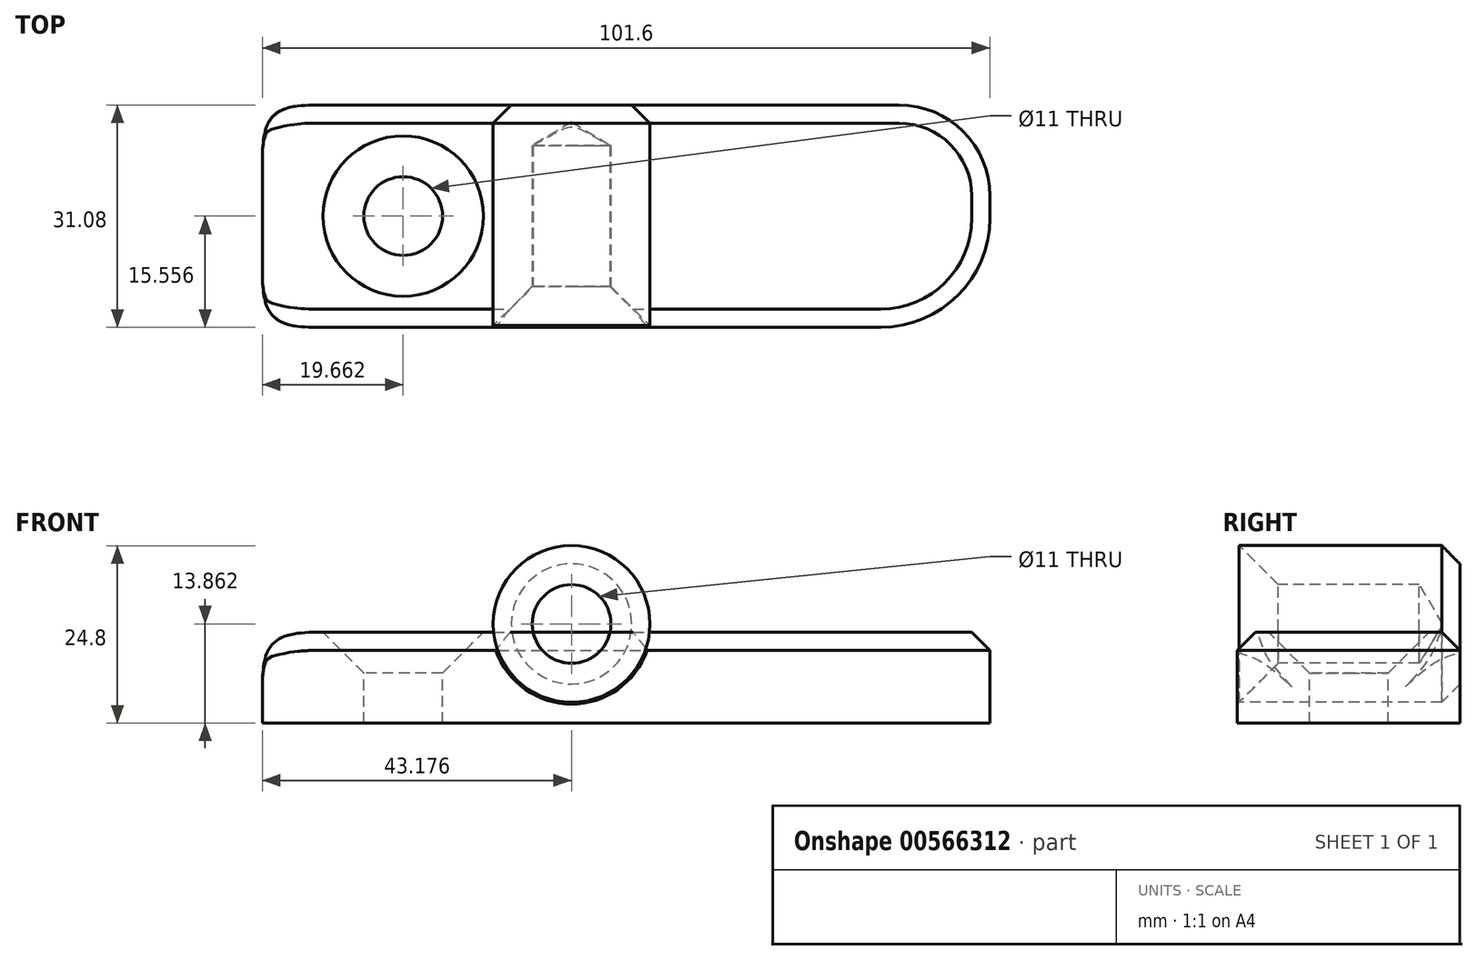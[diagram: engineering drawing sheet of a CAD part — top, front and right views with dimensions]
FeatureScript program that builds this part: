
annotation { "Feature Type Name" : "Feature", "Feature Type Description" : "" }
export const myFeature = defineFeature(function(context is Context, id is Id, definition is map)
    precondition{}
    {
        {
            var Q0;
            Q0=qCreatedBy(makeId("Top.planeOp"),FACE);
            var sketch = newSketch(context, id + "F0", { "sketchPlane" : qUnion([Q0])});
            skLineSegment(sketch, "E0.bottom", {"start": v(-114.14, 31.08) * mm, "end": v(-25.24, 31.08) * mm});
            skLineSegment(sketch, "E0.top", {"start": v(-114.14, 0) * mm, "end": v(-27.78, 0) * mm});
            skLineSegment(sketch, "E0.left", {"start": v(-114.14, 31.08) * mm, "end": v(-114.14, 0) * mm});
            skLineSegment(sketch, "E0.right", {"start": v(-12.54, 18.38) * mm, "end": v(-12.54, 15.24) * mm});
            skPoint(sketch, "E1.visualSharp", {"position": v(-12.54, 31.08) * mm});
            skArc(sketch, "E1.filletArc", {"start": v(-12.54, 18.38) * mm, "mid": v(-16.26, 27.36) * mm, "end": v(-25.24, 31.08) * mm});
            skPoint(sketch, "E2.visualSharp", {"position": v(-12.54, 0) * mm});
            skArc(sketch, "E2.filletArc", {"start": v(-27.78, 0) * mm, "mid": v(-17, 4.46) * mm, "end": v(-12.54, 15.24) * mm});
            skSolve(sketch);
        }
        {
            var Q0;
            Q0 = qSketchRegion(id + "F0", true);
            extrude(context, id + "F1", {"entities" : qUnion([Q0]), "depth" : 12.7 * mm, "offsetDistance" : 25.4 * mm});
        }
        {
            var Q0;
            Q0=makeQuery(id+"F1.opExtrude","SWEPT_FACE",FACE,{"disambiguationData":[OSD([sQuery(id+"F0.wireOp",EDGE,"E0.top")])]});
            var sketch = newSketch(context, id + "F2", { "sketchPlane" : qUnion([Q0])});
            skCircle(sketch, "E3", {"center": v(-70.96, 13.86) * mm, "radius": 10.94 * mm});
            skSolve(sketch);
        }
        {
            var Q0;
            {var subQ0=sQuery(id+"F2.wireOp",EDGE,"E3");var subQ1=makeQuery(id+"F1.opExtrude","CAP_EDGE",EDGE,{"disambiguationData":[OSD([sQuery(id+"F0.wireOp",EDGE,"E0.top")])],"isStart":false});var subQ2=makeQuery(id+"F2.imprint","INTERSECT",VERTEX,{"disambiguationData":[OD(0.0)],"derivedFrom":[subQ1,subQ0]});Q0=makeQuery(id+"F2.imprint","IMPRINT",FACE,{"disambiguationData":[TD([[makeQuery(id+"F2.imprint","IMPRINT",EDGE,{"disambiguationData":[TD([[subQ2,1.0]])],"derivedFrom":subQ0}),1.0]])]});}
            var Q1;
            {var subQ0=sQuery(id+"F2.wireOp",EDGE,"E3");var subQ1=makeQuery(id+"F1.opExtrude","CAP_EDGE",EDGE,{"disambiguationData":[OSD([sQuery(id+"F0.wireOp",EDGE,"E0.top")])],"isStart":false});var subQ2=makeQuery(id+"F2.imprint","INTERSECT",VERTEX,{"disambiguationData":[OD(0.0)],"derivedFrom":[subQ1,subQ0]});Q1=makeQuery(id+"F2.imprint","IMPRINT",FACE,{"disambiguationData":[TD([[makeQuery(id+"F2.imprint","IMPRINT",EDGE,{"disambiguationData":[TD([[subQ2,-1.0]])],"derivedFrom":subQ0}),1.0]])]});}
            var Q2;
            Q2=sQuery(id+"F2.wireOp",EDGE,"E3");
            var Q3;
            Q3=makeQuery(id+"F1.opExtrude","SWEPT_FACE",FACE,{"disambiguationData":[OSD([sQuery(id+"F0.wireOp",EDGE,"E0.bottom")])]});
            extrude(context, id + "F3", {"entities" : qUnion([Q0, Q1]), "surfaceEntities" : qUnion([Q2]), "endBound" : BoundingType.UP_TO_SURFACE, "oppositeDirection" : true, "depth" : 25.4 * mm, "endBoundEntityFace" : qUnion([Q3]), "offsetDistance" : 25.4 * mm});
        }
        {
            var Q0;
            Q0=sQuery(id+"F2.wireOp",VERTEX,"E3.center");
            var Q1;
            Q1=makeQuery(id+"F1.opExtrude","SWEPT_BODY",BODY,{"disambiguationData":[OSD([sQuery(id+"F0.wireOp",EDGE,"E0.bottom"),sQuery(id+"F0.wireOp",EDGE,"E0.top"),sQuery(id+"F0.wireOp",EDGE,"E0.left"),sQuery(id+"F0.wireOp",EDGE,"E0.right"),sQuery(id+"F0.wireOp",EDGE,"E1.filletArc"),sQuery(id+"F0.wireOp",EDGE,"E2.filletArc")])]});
            var Q2;
            Q2=makeQuery(id+"F3.opExtrude","SWEPT_BODY",BODY,{"disambiguationData":[OSD([sQuery(id+"F2.wireOp",EDGE,"E3")])]});
            hole(context, id + "F4", {"style" : HoleStyle.C_SINK, "endStyle" : HoleEndStyle.BLIND, "standardTappedOrClearance" : lookupTablePath({ "standard" : "ISO", "fit" : "Normal", "size" : "M10", "type" : "Clearance" }), "standardBlindInLast" : lookupTablePath({ "fit" : "Standard", "standard" : "ISO", "size" : "M10", "type" : "Clearance" }), "holeDiameter" : 11 * mm, "cSinkDiameter" : 22.4 * mm, "cSinkAngle" : 90 * degree, "holeDepth" : 25.4 * mm, "isTappedThrough" : true, "tappedDepth" : 12.7 * mm, "tapClearance" : 3, "locations" : qUnion([Q0]), "scope" : qUnion([Q1, Q2])});
        }
        {
            var Q0;
            Q0=makeQuery(id+"F1.opExtrude","CAP_EDGE",EDGE,{"disambiguationData":[OSD([sQuery(id+"F0.wireOp",EDGE,"E0.left")])],"isStart":false});
            var Q1;
            Q1=makeQuery(id+"F1.opExtrude","SWEPT_EDGE",EDGE,{"disambiguationData":[OSD([sQuery(id+"F0.wireOp",EDGE,"E0.top"),sQuery(id+"F0.wireOp",EDGE,"E0.left")])]});
            var Q2;
            Q2=makeQuery(id+"F1.opExtrude","SWEPT_EDGE",EDGE,{"disambiguationData":[OSD([sQuery(id+"F0.wireOp",EDGE,"E0.bottom"),sQuery(id+"F0.wireOp",EDGE,"E0.left")])]});
            fillet(context, id + "F5", {"entities" : qUnion([Q0, Q1, Q2]), "radius" : 7.62 * mm, "tangentPropagation" : true, "rho" : 0.6, "crossSection" : FilletCrossSection.CONIC, "allowEdgeOverflow" : false});
        }
        {
            var Q0;
            Q0=makeQuery(id+"F3.opExtrude","CAP_EDGE",EDGE,{"disambiguationData":[OSD([sQuery(id+"F2.wireOp",EDGE,"E3")])],"isStart":false});
            var Q1;
            {var subQ0=sQuery(id+"F0.wireOp",EDGE,"E0.left");var subQ1=sQuery(id+"F0.wireOp",EDGE,"E0.top");Q1=makeQuery(id+"F4.hole-0.boolean.opBoolean","SPLIT",EDGE,{"disambiguationData":[TD([makeQuery(id+"F1.opExtrude","SWEPT_FACE",FACE,{"disambiguationData":[OSD([subQ0])]})])],"derivedFrom":makeQuery(id+"F1.opExtrude","CAP_EDGE",EDGE,{"disambiguationData":[OSD([subQ1])],"isStart":false})});}
            var Q2;
            {var subQ0=sQuery(id+"F0.wireOp",EDGE,"E2.filletArc");var subQ1=sQuery(id+"F0.wireOp",EDGE,"E0.top");Q2=makeQuery(id+"F4.hole-0.boolean.opBoolean","SPLIT",EDGE,{"disambiguationData":[TD([makeQuery(id+"F1.opExtrude","SWEPT_FACE",FACE,{"disambiguationData":[OSD([subQ0])]})])],"derivedFrom":makeQuery(id+"F1.opExtrude","CAP_EDGE",EDGE,{"disambiguationData":[OSD([subQ1])],"isStart":false})});}
            chamfer(context, id + "F6", {"entities" : qUnion([Q0, Q1, Q2]), "width" : 2.54 * mm, "tangentPropagation" : true});
        }
        {
            var Q0;
            Q0=makeQuery(id+"F1.opExtrude","CAP_FACE",FACE,{"disambiguationData":[OSD([sQuery(id+"F0.wireOp",EDGE,"E0.bottom"),sQuery(id+"F0.wireOp",EDGE,"E0.top"),sQuery(id+"F0.wireOp",EDGE,"E0.left"),sQuery(id+"F0.wireOp",EDGE,"E0.right"),sQuery(id+"F0.wireOp",EDGE,"E1.filletArc"),sQuery(id+"F0.wireOp",EDGE,"E2.filletArc")])],"isStart":false});
            var sketch = newSketch(context, id + "F7", { "sketchPlane" : qUnion([Q0])});
            skLineSegment(sketch, "E4", {"start": v(-106.52, 15.56) * mm, "end": v(-47.07, 15.56) * mm});
            skCircle(sketch, "E5", {"center": v(-94.48, 15.56) * mm, "radius": 6.35 * mm});
            skSolve(sketch);
        }
        {
            var Q0;
            Q0=sQuery(id+"F7.wireOp",VERTEX,"E5.center");
            var Q1;
            Q1=makeQuery(id+"F1.opExtrude","SWEPT_BODY",BODY,{"disambiguationData":[OSD([sQuery(id+"F0.wireOp",EDGE,"E0.bottom"),sQuery(id+"F0.wireOp",EDGE,"E0.top"),sQuery(id+"F0.wireOp",EDGE,"E0.left"),sQuery(id+"F0.wireOp",EDGE,"E0.right"),sQuery(id+"F0.wireOp",EDGE,"E1.filletArc"),sQuery(id+"F0.wireOp",EDGE,"E2.filletArc")])]});
            hole(context, id + "F8", {"style" : HoleStyle.C_SINK, "endStyle" : HoleEndStyle.THROUGH, "standardTappedOrClearance" : lookupTablePath({ "standard" : "ISO", "fit" : "Normal", "size" : "M10", "type" : "Clearance" }), "standardBlindInLast" : lookupTablePath({ "fit" : "Standard", "standard" : "ISO", "size" : "M10", "type" : "Clearance" }), "holeDiameter" : 11 * mm, "cSinkDiameter" : 22.4 * mm, "cSinkAngle" : 90 * degree, "isTappedThrough" : true, "tappedDepth" : 12.7 * mm, "tapClearance" : 3, "locations" : qUnion([Q0]), "scope" : qUnion([Q1])});
        }
    });
